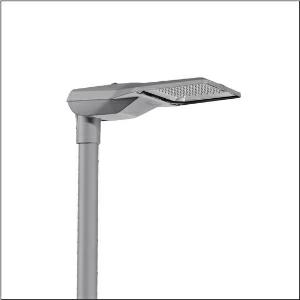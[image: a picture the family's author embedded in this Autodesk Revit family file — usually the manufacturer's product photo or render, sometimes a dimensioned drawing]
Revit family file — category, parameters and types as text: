
# Revit family: streetlight_sl_21_iq_midi___st1_0a_5xe3d31v08nb_ec4a
name_source: partatom
category: Lighting Fixtures
units: mm (PartAtom-declared; Revit-internal decimal feet)

## family parameters
Cut with Voids When Loaded = No
Host = Face
Light Source = No
Part Type = Normal
Room Calculation Point = No
Round Connector Dimension = Use Diameter
Shared = No

## types (1)
- --- (1 x LED, 21550 lm, 136.6 W, 3000K)
    Apparent Load = 137 VA
    CIE Flux Codes = 40 73 97 100 100
    Color Rendering = 70
    Color Temperature = 3000K
    Default Elevation = 1800 mm
    Description = Streetlight SL 21 iQ midi, mast luminaire, primary light control with lens, of PMMA, primary optical cover: cover, of toughened safety glass, transparent, light distribution: ST1.0a, light emission: direct distribution, primary light characteristic: asymmetric, installation type: post-top, side-entry, LED, High Power LED, rated luminous flux: 21.550lm, luminous efficacy: 158lm/W, light colour: 730, colour temperature: 3000K, control: presetting dimming logarithmic, Street-Remote, Auto-Match, Temp-Guard, Lumen-Switch, Night-Set, Smart-Wire, Light-Fading, Desk-Remote (wireless, voltage-free reading and setting of iQ features in the workshop via application-optimized NFC function/RFID function), optimised constant luminous flux control (CLO 2.0), mains connection: 230..240V, AC, 50/60Hz, start of lifetime: 137W, end of service life: 144W, reduction: 61W, luminaire housing, of diecast aluminium, powder-coated, Siteco® metallic grey (DB 702S), corrosivity category C5 mid according to DIN EN ISO 12944, please order mast flange separately, inclination adjustable: 0°, 5°, 10°, 15°, sealing non-destructively replaceable, multi-level sealing system, length: 644mm, width: 335mm, height: 110mm, mast flange for spigot size: 42mm (side-entry): 5XC10008XM4, 60/48mm (side-entry/post-top): 5XC10108XM2, 76/60mm (side-entry/post-top): 5XC10108XM1, Smart Interface above, protection rating (complete): IP66, insulation class (complete): insulation class II (safety insulation), certification: CE, ENEC, ENEC+, VDE, impact resistance: IK09, permissible operating ambient temperature for outdoor applications: -40..+50°C, standard-compliant lighting for roads and squares, packaging unit: 1 piece

Light Distribution: ST1.0a
    Height = 111 mm
    Lamp = 1 x LED
    Lamp Light Flux = 21550 lm
    Lamp Power = 136.6 W
    Lamp count = 1
    Length = 644 mm
    Luminous efficacy = 158 lm/W
    Manufacturer = Siteco
    ModVariant = No
    Model = 5XE3D31V08NB
    Number of Poles = 1
    OnlyDefault = Yes
    Power Factor = 1
    Product Name = Streetlight SL 21 iQ midi | ST1.0a
    Product group = mast luminaire | pylon top
    ProductGroupID = 6100
    Protection Class = Protection class II
    Protection Degree = IP 66
    RLX_Detail_Level = 1
    RLX_Emergency_Light_Flux = 0 lm
    RLX_Emergency_Type = 0
    RLX_Emergency_Type_DB = No
    RlxData = <blob elided: 91069 chars, md5=eda49951>
    Socket = socket
    Standby Power = 0 W
    System Light Flux = 21550 lm
    System Power = 137 W
    Type Comments = factory setting: luminous flux: 100 % | dim-lin: 254 | 733 mA
    Type Image = l_1004302.jpg
    URL = http://relux.com
    VarID = @adj_062117
    Voltage = 0 V
    Weight = 0.00 kg
    Width = 336 mm

## geometry (parser evidence)
native form markers: Blend x4, Sweep x11
no freeform markers — native parametric forms only
